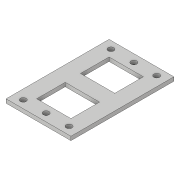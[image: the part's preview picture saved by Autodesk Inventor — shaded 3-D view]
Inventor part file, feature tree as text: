
AUTODESK INVENTOR PART (.ipt)
format: ipt  version: 2018 (Build 220112000, 112)  size: 113,664 bytes
history: native  units: in
note: dims shown in document units (in); Inventor stores cm internally (conversion verified against a paired STEP export)
features: extrude x2, sketch x2, hole x1, pattern_linear x1
ambient origin geometry x8: Origin, YZ Plane, XZ Plane, XY Plane, X Axis, Y Axis, Z Axis, Center Point
bodies: Solid1 (feature_tree)
feature tree (6):
  extrude  "Extrusion1"  Depth=21.2598in
  extrude  "Extrusion2"  Depth=5.9in
  hole  "Hole1"  [1 undecoded]
  pattern_linear  "Rectangular Pattern1"  Spacing1=7.08in  [1 undecoded]
  sketch  "Sketch1"  dims[d0=13.3858in d1=21.2598in]
  sketch  "Sketch2"  dims[d2=0.7875in d3=0.0in d4=5.9in d5=5.9in d6=7.08in d7=7.08in d9=3.149in d10=0.7875in d11=0.0in d12=1.575in d13=1.9685in d14=1.1811in d15=0.75in d16=0.375in d17=0.25in d18=0.5635in d19=1.0in d20=0.8108in d21=0.7874in d23=18.11in d24=1.1811in d26=4.7244in]
note: 2 required parameter values undecoded (feature->parameter linkage not recoverable at this tier; creation-order binding heuristic only, values carry confidence <= 0.55)
